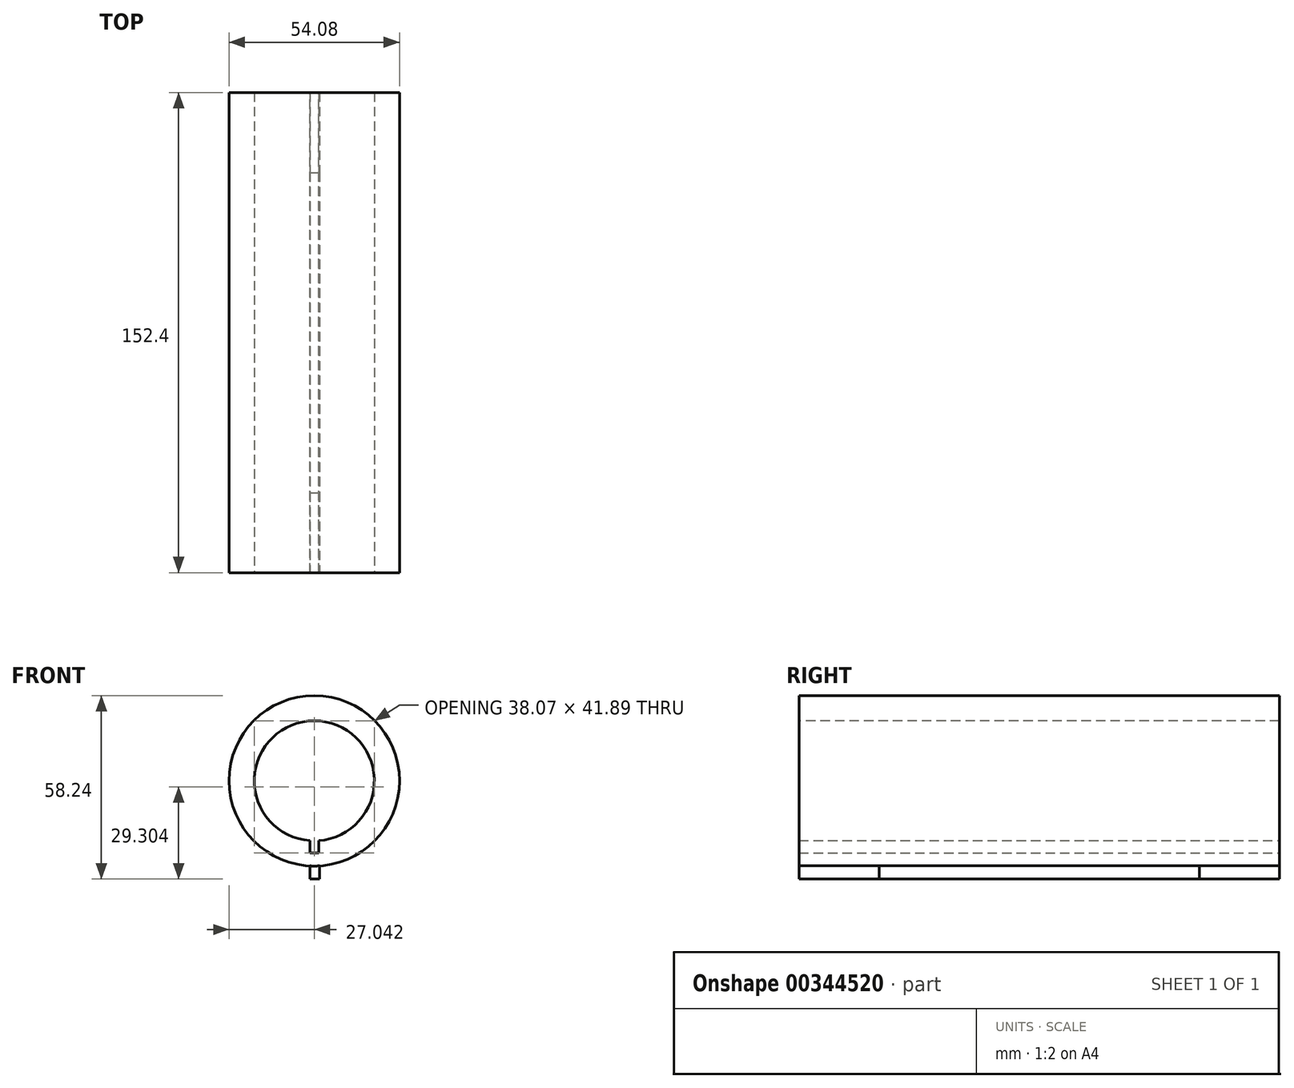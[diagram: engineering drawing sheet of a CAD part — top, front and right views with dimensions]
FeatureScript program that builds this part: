
annotation { "Feature Type Name" : "Feature", "Feature Type Description" : "" }
export const myFeature = defineFeature(function(context is Context, id is Id, definition is map)
    precondition{}
    {
        {
            var Q0;
            Q0=qCreatedBy(makeId("Front.planeOp"),FACE);
            var sketch = newSketch(context, id + "F0", { "sketchPlane" : qUnion([Q0])});
            skCircle(sketch, "E0", {"center": v(27.64, 27.88) * mm, "radius": 27.04 * mm});
            skSolve(sketch);
        }
        {
            var Q0;
            Q0=makeQuery(id+"F0.imprint","IMPRINT",FACE,{"disambiguationData":[TD([[makeQuery(id+"F0.imprint","IMPRINT",EDGE,{"derivedFrom":sQuery(id+"F0.wireOp",EDGE,"E0")}),1.0]])]});
            extrude(context, id + "F1", {"entities" : qUnion([Q0]), "depth" : 25.4 * mm});
        }
        {
            var Q0;
            Q0=makeQuery(id+"F1.opExtrude","CAP_FACE",FACE,{"disambiguationData":[OSD([sQuery(id+"F0.wireOp",EDGE,"E0")])],"isStart":false});
            var sketch = newSketch(context, id + "F2", { "sketchPlane" : qUnion([Q0])});
            skPoint(sketch, "E1", {"position": v(27.64, 27.88) * mm});
            skSolve(sketch);
        }
        {
            var Q0;
            Q0=sQuery(id+"F2.wireOp",VERTEX,"E1");
            var Q1;
            Q1=makeQuery(id+"F1.opExtrude","SWEPT_BODY",BODY,{"disambiguationData":[OSD([sQuery(id+"F0.wireOp",EDGE,"E0")])]});
            hole(context, id + "F3", {"style" : HoleStyle.SIMPLE, "endStyle" : HoleEndStyle.THROUGH, "holeDiameter" : 38.1 * mm, "isTappedThrough" : true, "tappedDepth" : 12.7 * mm, "tapClearance" : 3, "locations" : qUnion([Q0]), "scope" : qUnion([Q1])});
        }
        {
            var Q0;
            Q0=makeQuery(id+"F1.opExtrude","CAP_FACE",FACE,{"disambiguationData":[OSD([sQuery(id+"F0.wireOp",EDGE,"E0")])],"isStart":true});
            var sketch = newSketch(context, id + "F4", { "sketchPlane" : qUnion([Q0])});
            skLineSegment(sketch, "E2.bottom", {"start": v(-26.25, 8.88) * mm, "end": v(-29.02, 8.88) * mm});
            skLineSegment(sketch, "E2.top", {"start": v(-26.25, 5.04) * mm, "end": v(-29.02, 5.04) * mm});
            skLineSegment(sketch, "E2.left", {"start": v(-26.25, 8.88) * mm, "end": v(-26.25, 5.04) * mm});
            skLineSegment(sketch, "E2.right", {"start": v(-29.02, 8.88) * mm, "end": v(-29.02, 5.04) * mm});
            skSolve(sketch);
        }
        {
            var Q0;
            {var subQ0=sQuery(id+"F4.wireOp",EDGE,"E2.top");Q0=makeQuery(id+"F4.imprint","IMPRINT",FACE,{"disambiguationData":[TD([[makeQuery(id+"F4.imprint","IMPRINT",EDGE,{"derivedFrom":subQ0}),-1.0]])]});}
            extrude(context, id + "F5", {"entities" : qUnion([Q0]), "operationType" : NewBodyOperationType.REMOVE, "oppositeDirection" : true, "depth" : 25.4 * mm});
        }
        {
            var Q0;
            Q0=makeQuery(id+"F1.opExtrude","CAP_FACE",FACE,{"disambiguationData":[OSD([sQuery(id+"F0.wireOp",EDGE,"E0")])],"isStart":false});
            extrude(context, id + "F6", {"entities" : qUnion([Q0]), "operationType" : NewBodyOperationType.ADD, "depth" : 127 * mm});
        }
        {
            var Q0;
            Q0=makeQuery(id+"F6.opExtrude","CAP_FACE",FACE,{"disambiguationData":[OSD([sQuery(id+"F0.wireOp",EDGE,"E0")])],"isStart":false});
            var sketch = newSketch(context, id + "F7", { "sketchPlane" : qUnion([Q0])});
            skLineSegment(sketch, "E3.bottom", {"start": v(26.25, 0.87) * mm, "end": v(29.28, 0.87) * mm});
            skLineSegment(sketch, "E3.top", {"start": v(26.25, -3.32) * mm, "end": v(29.28, -3.32) * mm});
            skLineSegment(sketch, "E3.left", {"start": v(26.25, 0.87) * mm, "end": v(26.25, -3.32) * mm});
            skLineSegment(sketch, "E3.right", {"start": v(29.28, 0.87) * mm, "end": v(29.28, -3.32) * mm});
            skSolve(sketch);
        }
        {
            var Q0;
            Q0=makeQuery(id+"F7.imprint","IMPRINT",FACE,{"disambiguationData":[TD([[makeQuery(id+"F7.imprint","IMPRINT",EDGE,{"derivedFrom":sQuery(id+"F7.wireOp",EDGE,"E3.top")}),1.0]])]});
            extrude(context, id + "F8", {"entities" : qUnion([Q0]), "oppositeDirection" : true, "depth" : 25.4 * mm});
        }
        {
            var Q0;
            Q0=makeQuery(id+"F8.opExtrude","CAP_FACE",FACE,{"disambiguationData":[OSD([sQuery(id+"F0.wireOp",EDGE,"E0"),sQuery(id+"F7.wireOp",EDGE,"E3.bottom"),sQuery(id+"F7.wireOp",EDGE,"E3.top"),sQuery(id+"F7.wireOp",EDGE,"E3.left"),sQuery(id+"F7.wireOp",EDGE,"E3.right")])],"isStart":false});
            extrude(context, id + "F9", {"entities" : qUnion([Q0]), "depth" : 101.6 * mm});
        }
        {
            var Q0;
            Q0=makeQuery(id+"F9.opExtrude","CAP_FACE",FACE,{"disambiguationData":[OSD([sQuery(id+"F0.wireOp",EDGE,"E0"),sQuery(id+"F7.wireOp",EDGE,"E3.bottom"),sQuery(id+"F7.wireOp",EDGE,"E3.top"),sQuery(id+"F7.wireOp",EDGE,"E3.left"),sQuery(id+"F7.wireOp",EDGE,"E3.right")])],"isStart":false});
            extrude(context, id + "F10", {"entities" : qUnion([Q0]), "depth" : 25.4 * mm});
        }
    });
